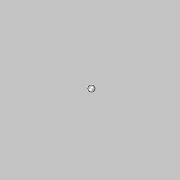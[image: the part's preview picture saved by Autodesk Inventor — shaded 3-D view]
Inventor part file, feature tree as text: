
AUTODESK INVENTOR PART (.ipt)
format: ipt  version: 2017 (Build 210142000, 142)  size: 121,344 bytes
history: native  units: mm
features: other x10, sketch x3, extrude x3, mirror x2, sweep x1, plane x1, pattern_circular x1, projected_geometry x1
ambient origin geometry x7: Origin, YZ Plane, XZ Plane, X Axis, Y Axis, Z Axis, Center Point
bodies: Solid1 (feature_tree), Solid2 (feature_tree)
feature tree (22):
  other  "Table"
  other  "CableLadderTeeKHJZP-150"
  other  "CableLadderTeeKHJZP-200"
  other  "CableLadderTeeKHJZP-300"
  other  "CableLadderTeeKHJZP-400"
  other  "CableLadderTeeKHJZP-500"
  other  "CableLadderTeeKHJZP-600"
  other  "CableLadderTeeKHJZP-800"
  other  "CableLadderTeeKHJZP-1000"
  sketch  "Sketch4"  dims[d0=55.0mm d1=18.0mm]
  sweep  "Sweep1"
  plane  "Work Plane1"
  mirror  "Mirror2"
  extrude  "Extrusion3"  Depth=18.0mm
  extrude  "Extrusion2"  Depth=268.0mm
  pattern_circular  "Circular Pattern1"  Count=40  [1 undecoded]
  extrude  "Extrusion4"  TaperAngle=0.0deg  [1 undecoded]
  mirror  "Mirror3"
  other  "XY Ground Plane"
  sketch  "Sketch6"  dims[d5=30.0mm d6=18.0mm]
  projected_geometry  "Projected Loop1"
  sketch  "Sketch7"  dims[d7=3000.0mm d8=0.0mm d14=268.0mm d16=400.0mm d17=0.0mm d18=0.0mm d20=20.0mm d21=90.0deg d23=-148.5mm d24=10.0mm d25=0.0mm d26=10.0mm d27=0.0mm d29=0.0mm]
note: 2 required parameter values undecoded (feature->parameter linkage not recoverable at this tier; creation-order binding heuristic only, values carry confidence <= 0.55)
